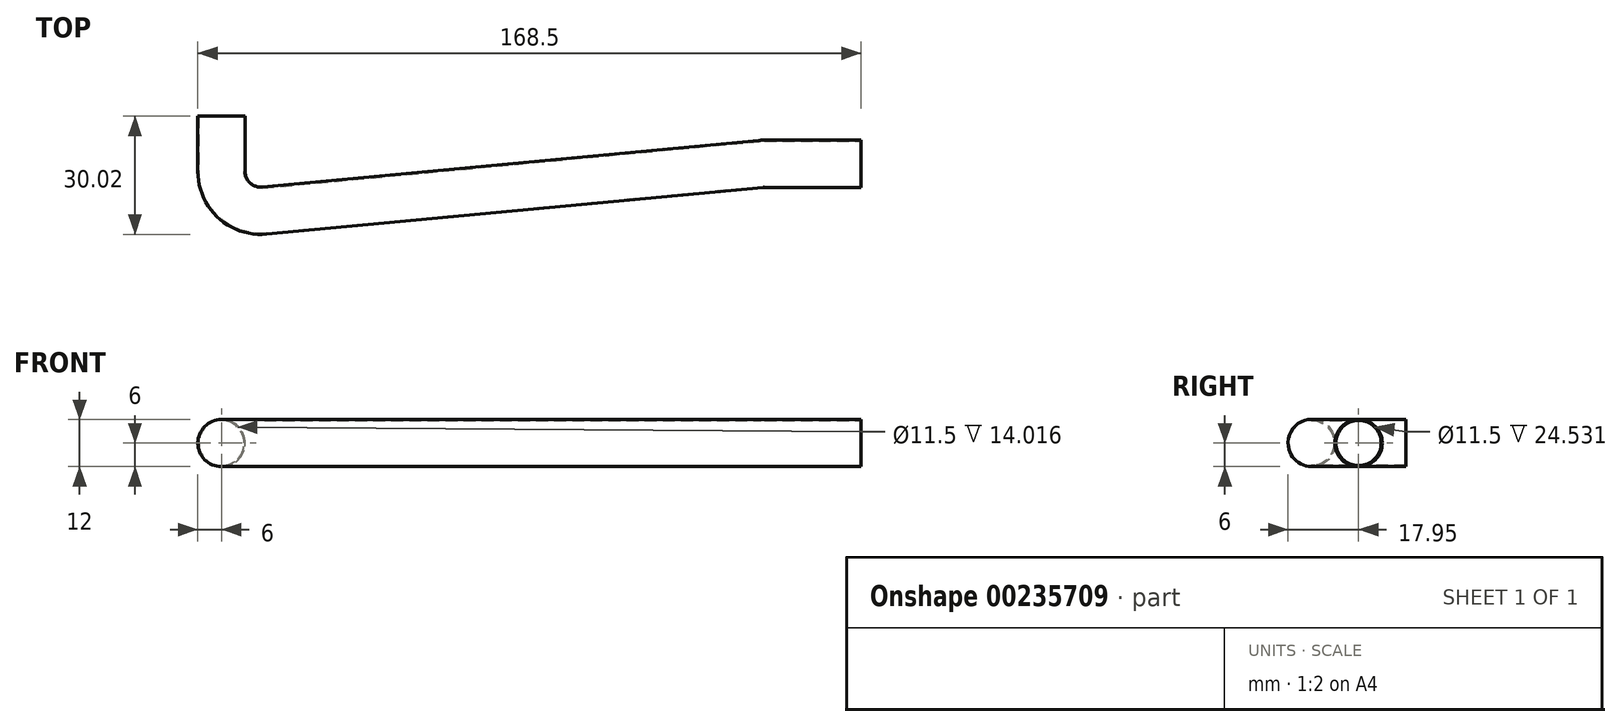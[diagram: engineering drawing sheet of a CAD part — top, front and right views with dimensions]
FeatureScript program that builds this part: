
annotation { "Feature Type Name" : "Feature", "Feature Type Description" : "" }
export const myFeature = defineFeature(function(context is Context, id is Id, definition is map)
    precondition{}
    {
        {
            var Q0;
            Q0=qCreatedBy(makeId("Top.planeOp"),FACE);
            var sketch = newSketch(context, id + "F0", { "sketchPlane" : qUnion([Q0])});
            skLineSegment(sketch, "E0", {"start": v(0, 10.98) * mm, "end": v(0, 25) * mm});
            skLineSegment(sketch, "E1", {"start": v(0, 0) * mm, "end": v(162.5, 0) * mm, "construction": true});
            skLineSegment(sketch, "E2", {"start": v(162.5, 0) * mm, "end": v(162.5, 12.93) * mm, "construction": true});
            skLineSegment(sketch, "E3", {"start": v(162.5, 12.93) * mm, "end": v(137.97, 12.93) * mm});
            skLineSegment(sketch, "E4", {"start": v(137.03, 12.89) * mm, "end": v(10.94, 1.03) * mm});
            skPoint(sketch, "E5.visualSharp", {"position": v(0, 0) * mm});
            skArc(sketch, "E5.filletArc", {"start": v(0, 10.98) * mm, "mid": v(3.27, 3.59) * mm, "end": v(10.94, 1.03) * mm});
            skPoint(sketch, "E6.visualSharp", {"position": v(137.5, 12.93) * mm});
            skArc(sketch, "E6.filletArc", {"start": v(137.97, 12.93) * mm, "mid": v(137.5, 12.92) * mm, "end": v(137.03, 12.89) * mm});
            skLineSegment(sketch, "E7.0", {"start": v(5.75, 10.98) * mm, "end": v(5.75, 25) * mm});
            skLineSegment(sketch, "E7.1", {"start": v(162.5, 18.68) * mm, "end": v(137.97, 18.68) * mm});
            skArc(sketch, "E7.2", {"start": v(137.97, 18.68) * mm, "mid": v(137.23, 18.66) * mm, "end": v(136.5, 18.61) * mm});
            skLineSegment(sketch, "E7.3", {"start": v(136.5, 18.61) * mm, "end": v(10.4, 6.75) * mm});
            skArc(sketch, "E7.4", {"start": v(5.75, 10.98) * mm, "mid": v(7.14, 7.84) * mm, "end": v(10.4, 6.75) * mm});
            skLineSegment(sketch, "E8.0", {"start": v(6, 10.98) * mm, "end": v(6, 25) * mm});
            skLineSegment(sketch, "E8.1", {"start": v(162.5, 18.93) * mm, "end": v(137.97, 18.93) * mm});
            skArc(sketch, "E8.2", {"start": v(137.97, 18.93) * mm, "mid": v(137.22, 18.91) * mm, "end": v(136.47, 18.86) * mm});
            skLineSegment(sketch, "E8.3", {"start": v(136.47, 18.86) * mm, "end": v(10.37, 7) * mm});
            skArc(sketch, "E8.4", {"start": v(6, 10.98) * mm, "mid": v(7.3, 8.03) * mm, "end": v(10.37, 7) * mm});
            skLineSegment(sketch, "E9.0", {"start": v(-5.75, 10.98) * mm, "end": v(-5.75, 25) * mm});
            skLineSegment(sketch, "E9.1", {"start": v(162.5, 7.18) * mm, "end": v(137.97, 7.18) * mm});
            skArc(sketch, "E9.2", {"start": v(137.97, 7.18) * mm, "mid": v(137.77, 7.18) * mm, "end": v(137.57, 7.16) * mm});
            skLineSegment(sketch, "E9.3", {"start": v(137.57, 7.16) * mm, "end": v(11.47, -4.7) * mm});
            skArc(sketch, "E9.4", {"start": v(-5.75, 10.98) * mm, "mid": v(-0.6, -0.66) * mm, "end": v(11.47, -4.7) * mm});
            skLineSegment(sketch, "E10.0", {"start": v(-6, 10.98) * mm, "end": v(-6, 25) * mm});
            skLineSegment(sketch, "E10.1", {"start": v(162.5, 6.93) * mm, "end": v(137.97, 6.93) * mm});
            skArc(sketch, "E10.2", {"start": v(137.97, 6.93) * mm, "mid": v(137.78, 6.93) * mm, "end": v(137.6, 6.91) * mm});
            skLineSegment(sketch, "E10.3", {"start": v(137.6, 6.91) * mm, "end": v(11.5, -4.95) * mm});
            skArc(sketch, "E10.4", {"start": v(-6, 10.98) * mm, "mid": v(-0.77, -0.85) * mm, "end": v(11.5, -4.95) * mm});
            skLineSegment(sketch, "E11", {"start": v(-6, 25) * mm, "end": v(-5.75, 25) * mm});
            skLineSegment(sketch, "E12", {"start": v(5.75, 25) * mm, "end": v(6, 25) * mm});
            skLineSegment(sketch, "E13", {"start": v(162.5, 18.93) * mm, "end": v(162.5, 18.68) * mm});
            skLineSegment(sketch, "E14", {"start": v(162.5, 6.93) * mm, "end": v(162.5, 7.18) * mm});
            skSolve(sketch);
        }
        {
            var Q0;
            Q0=qCreatedBy(makeId("Front.planeOp"),FACE);
            cPlane(context, id + "F1", {"entities" : qUnion([Q0]), "cplaneType" : CPlaneType.OFFSET, "offset" : 25 * mm, "oppositeDirection" : true, "width" : 150 * mm, "height" : 150 * mm});
        }
        {
            var Q0;
            Q0=qCreatedBy(id+"F1.planeOp",FACE);
            var sketch = newSketch(context, id + "F2", { "sketchPlane" : qUnion([Q0])});
            skCircle(sketch, "E15", {"center": v(0, 0) * mm, "radius": 5.75 * mm});
            skCircle(sketch, "E16", {"center": v(0, 0) * mm, "radius": 6 * mm});
            skSolve(sketch);
        }
        {
            var Q0;
            Q0=makeQuery(id+"F2.imprint","IMPRINT",FACE,{"disambiguationData":[TD([[makeQuery(id+"F2.imprint","IMPRINT",EDGE,{"derivedFrom":sQuery(id+"F2.wireOp",EDGE,"E15")}),-1.0]])]});
            var Q1;
            Q1=sQuery(id+"F0.wireOp",EDGE,"E10.0");
            var Q2;
            Q2=sQuery(id+"F0.wireOp",EDGE,"E10.4");
            var Q3;
            Q3=sQuery(id+"F0.wireOp",EDGE,"E10.3");
            var Q4;
            Q4=sQuery(id+"F0.wireOp",EDGE,"E10.1");
            var Q5;
            Q5=sQuery(id+"F0.wireOp",EDGE,"E10.2");
            sweep(context, id + "F3", {"profiles" : qUnion([Q0]), "path" : qUnion([Q1, Q2, Q3, Q4, Q5])});
        }
    });
